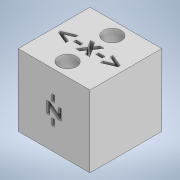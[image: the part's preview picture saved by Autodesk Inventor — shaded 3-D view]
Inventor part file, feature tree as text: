
AUTODESK INVENTOR PART (.ipt)
format: ipt  version: 2021 (Build 250183000, 183)  size: 176,640 bytes
history: native  units: in
note: dims shown in document units (in); Inventor stores cm internally (conversion verified against a paired STEP export)
features: extrude x4, sketch x4
ambient origin geometry x8: Origin, YZ Plane, XZ Plane, XY Plane, X Axis, Y Axis, Z Axis, Center Point
bodies: Solid1 (feature_tree)
feature tree (8):
  extrude  "Extrusion1"  Depth=1.0in
  extrude  "Extrusion2"  Depth=0.2in TaperAngle=0.0deg
  extrude  "Extrusion3"  Depth=0.2in
  extrude  "Extrusion4"  Depth=1.0in
  sketch  "Sketch1"  dims[d0=1.0in d1=1.0in]
  sketch  "Sketch2"  dims[d2=1.0in d3=0.0in d4=0.2in d5=0.0in]
  sketch  "Sketch3"  dims[d6=0.2in d7=0.0in d46=0.0063in]
  sketch  "Sketch11"  dims[d48=60.0deg d67=0.0063in d69=60.0deg d81=0.25in d82=0.1875in d83=0.1875in d84=1.0in d85=0.0in d99=0.0063in d101=60.0deg d120=0.0063in d122=60.0deg d143=0.3779in d161=0.3779in]
